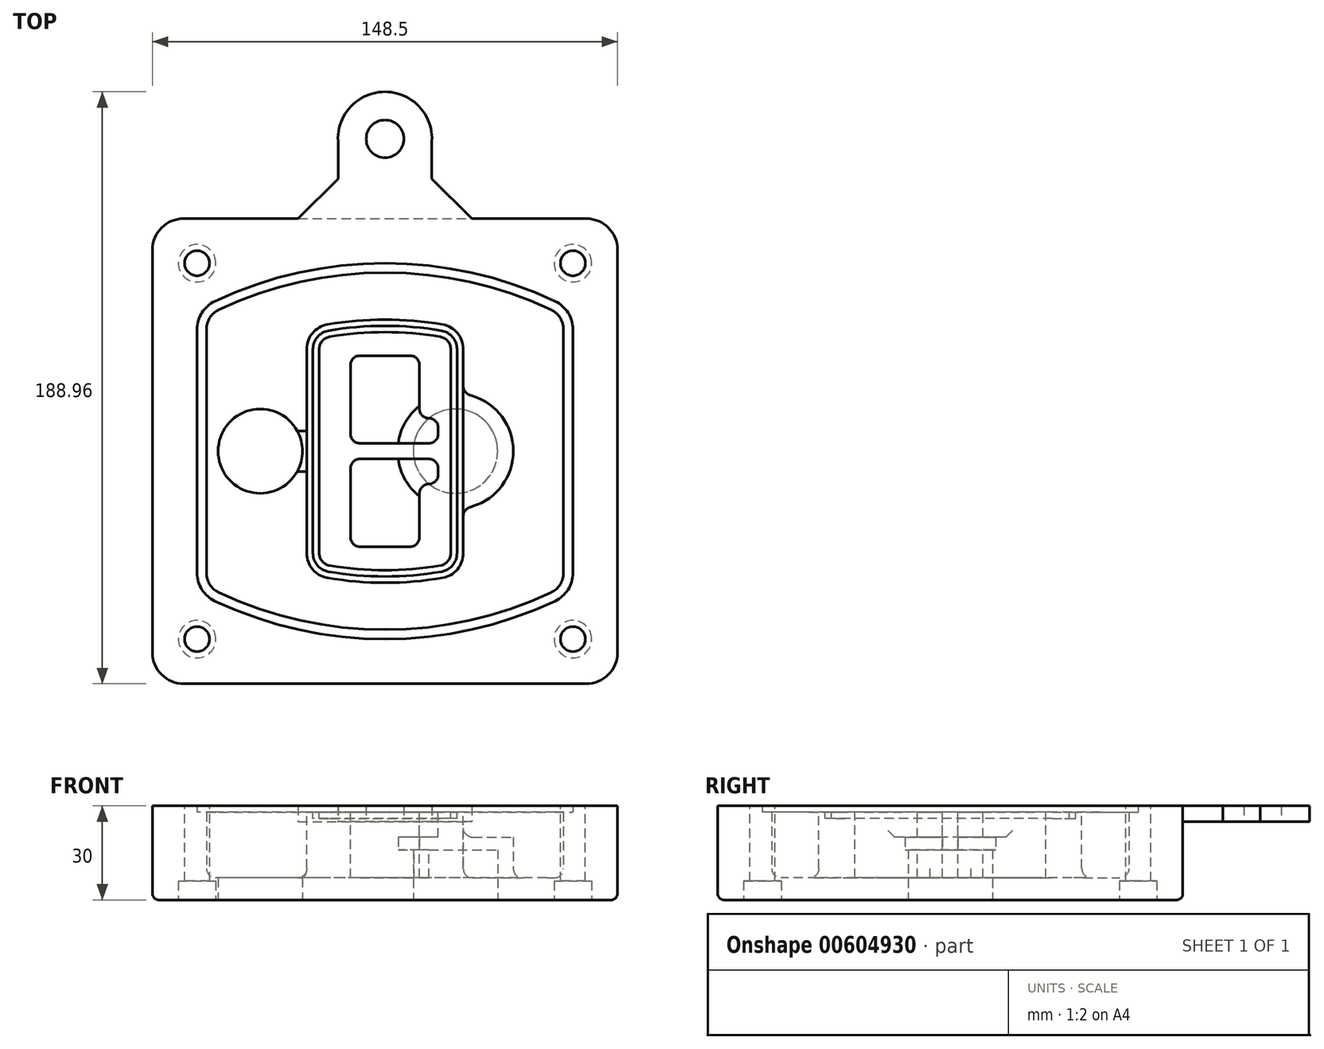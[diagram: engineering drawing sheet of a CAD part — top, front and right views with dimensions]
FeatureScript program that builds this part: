
annotation { "Feature Type Name" : "Feature", "Feature Type Description" : "" }
export const myFeature = defineFeature(function(context is Context, id is Id, definition is map)
    precondition{}
    {
        {
            var Q0;
            Q0=qCreatedBy(makeId("Top.planeOp"),FACE);
            var sketch = newSketch(context, id + "F0", { "sketchPlane" : qUnion([Q0])});
            skPoint(sketch, "E0.rect.middle", {"position": v(0, 0) * mm});
            skLineSegment(sketch, "E1.bottom", {"start": v(-64.25, -74.25) * mm, "end": v(64.25, -74.25) * mm});
            skLineSegment(sketch, "E1.top", {"start": v(-64.25, 74.25) * mm, "end": v(64.25, 74.25) * mm});
            skLineSegment(sketch, "E1.left", {"start": v(-74.25, -64.25) * mm, "end": v(-74.25, 64.25) * mm});
            skLineSegment(sketch, "E1.right", {"start": v(74.25, -64.25) * mm, "end": v(74.25, 64.25) * mm});
            skLineSegment(sketch, "E2", {"start": v(-74.25, 74.25) * mm, "end": v(74.25, -74.25) * mm, "construction": true});
            skLineSegment(sketch, "E3", {"start": v(74.25, 74.25) * mm, "end": v(-74.25, -74.25) * mm, "construction": true});
            skCircle(sketch, "E4", {"center": v(-60, 60) * mm, "radius": 4 * mm});
            skCircle(sketch, "E5", {"center": v(60, 60) * mm, "radius": 4 * mm});
            skCircle(sketch, "E6", {"center": v(60, -60) * mm, "radius": 4 * mm});
            skCircle(sketch, "E7", {"center": v(-60, -60) * mm, "radius": 4 * mm});
            skLineSegment(sketch, "E8", {"start": v(-60, 60) * mm, "end": v(60, 60) * mm, "construction": true});
            skLineSegment(sketch, "E9", {"start": v(60, 60) * mm, "end": v(60, -60) * mm, "construction": true});
            skLineSegment(sketch, "E10", {"start": v(60, -60) * mm, "end": v(-60, -60) * mm, "construction": true});
            skLineSegment(sketch, "E11", {"start": v(-60, -60) * mm, "end": v(-60, 60) * mm, "construction": true});
            skLineSegment(sketch, "E12", {"start": v(-60, 38.83) * mm, "end": v(-60, -38.83) * mm});
            skLineSegment(sketch, "E13", {"start": v(60, 38.83) * mm, "end": v(60, -38.83) * mm});
            skArc(sketch, "E14", {"start": v(54.26, 47.88) * mm, "mid": v(0, 60) * mm, "end": v(-54.26, 47.88) * mm});
            skArc(sketch, "E15", {"start": v(-54.26, -47.88) * mm, "mid": v(0, -60) * mm, "end": v(54.26, -47.88) * mm});
            skLineSegment(sketch, "E16", {"start": v(-60, 0) * mm, "end": v(60, 0) * mm, "construction": true});
            skPoint(sketch, "E17.visualSharp", {"position": v(-60, -45) * mm});
            skArc(sketch, "E17.filletArc", {"start": v(-60, -38.83) * mm, "mid": v(-58.44, -44.2) * mm, "end": v(-54.26, -47.88) * mm});
            skPoint(sketch, "E18.visualSharp", {"position": v(-60, 45) * mm});
            skArc(sketch, "E18.filletArc", {"start": v(-54.26, 47.88) * mm, "mid": v(-58.44, 44.2) * mm, "end": v(-60, 38.83) * mm});
            skPoint(sketch, "E19.visualSharp", {"position": v(60, 45) * mm});
            skArc(sketch, "E19.filletArc", {"start": v(60, 38.83) * mm, "mid": v(58.44, 44.2) * mm, "end": v(54.26, 47.88) * mm});
            skPoint(sketch, "E20.visualSharp", {"position": v(60, -45) * mm});
            skArc(sketch, "E20.filletArc", {"start": v(54.26, -47.88) * mm, "mid": v(58.44, -44.2) * mm, "end": v(60, -38.83) * mm});
            skPoint(sketch, "E21.visualSharp", {"position": v(-74.25, 74.25) * mm});
            skArc(sketch, "E21.filletArc", {"start": v(-64.25, 74.25) * mm, "mid": v(-71.32, 71.32) * mm, "end": v(-74.25, 64.25) * mm});
            skPoint(sketch, "E22.visualSharp", {"position": v(74.25, 74.25) * mm});
            skArc(sketch, "E22.filletArc", {"start": v(74.25, 64.25) * mm, "mid": v(71.32, 71.32) * mm, "end": v(64.25, 74.25) * mm});
            skPoint(sketch, "E23.visualSharp", {"position": v(74.25, -74.25) * mm});
            skArc(sketch, "E23.filletArc", {"start": v(64.25, -74.25) * mm, "mid": v(71.32, -71.32) * mm, "end": v(74.25, -64.25) * mm});
            skPoint(sketch, "E24.visualSharp", {"position": v(-74.25, -74.25) * mm});
            skArc(sketch, "E24.filletArc", {"start": v(-74.25, -64.25) * mm, "mid": v(-71.32, -71.32) * mm, "end": v(-64.25, -74.25) * mm});
            skArc(sketch, "E25.0", {"start": v(57, 38.83) * mm, "mid": v(55.9, 42.58) * mm, "end": v(52.98, 45.17) * mm});
            skLineSegment(sketch, "E25.1", {"start": v(57, 38.83) * mm, "end": v(57, -38.83) * mm});
            skArc(sketch, "E25.2", {"start": v(52.98, -45.17) * mm, "mid": v(55.9, -42.58) * mm, "end": v(57, -38.83) * mm});
            skArc(sketch, "E25.3", {"start": v(-52.98, -45.17) * mm, "mid": v(0, -57) * mm, "end": v(52.98, -45.17) * mm});
            skArc(sketch, "E25.4", {"start": v(-57, -38.83) * mm, "mid": v(-55.9, -42.58) * mm, "end": v(-52.98, -45.17) * mm});
            skArc(sketch, "E25.5", {"start": v(52.98, 45.17) * mm, "mid": v(0, 57) * mm, "end": v(-52.98, 45.17) * mm});
            skLineSegment(sketch, "E25.6", {"start": v(-57, 38.83) * mm, "end": v(-57, -38.83) * mm});
            skArc(sketch, "E25.7", {"start": v(-52.98, 45.17) * mm, "mid": v(-55.9, 42.58) * mm, "end": v(-57, 38.83) * mm});
            skArc(sketch, "E26.0", {"start": v(-55.96, 51.5) * mm, "mid": v(-61.82, 46.33) * mm, "end": v(-64, 38.83) * mm});
            skArc(sketch, "E26.1", {"start": v(55.96, 51.5) * mm, "mid": v(0, 64) * mm, "end": v(-55.96, 51.5) * mm});
            skArc(sketch, "E26.2", {"start": v(64, 38.83) * mm, "mid": v(61.82, 46.33) * mm, "end": v(55.96, 51.5) * mm});
            skLineSegment(sketch, "E26.3", {"start": v(64, 38.83) * mm, "end": v(64, -38.83) * mm});
            skArc(sketch, "E26.4", {"start": v(55.96, -51.5) * mm, "mid": v(61.82, -46.33) * mm, "end": v(64, -38.83) * mm});
            skLineSegment(sketch, "E26.5", {"start": v(-64, 38.83) * mm, "end": v(-64, -38.83) * mm});
            skArc(sketch, "E26.6", {"start": v(-55.96, -51.5) * mm, "mid": v(0, -64) * mm, "end": v(55.96, -51.5) * mm});
            skArc(sketch, "E26.7", {"start": v(-64, -38.83) * mm, "mid": v(-61.82, -46.33) * mm, "end": v(-55.96, -51.5) * mm});
            skSolve(sketch);
        }
        {
            var Q0;
            Q0=makeQuery(id+"F0.imprint","IMPRINT",FACE,{"disambiguationData":[TD([[makeQuery(id+"F0.imprint","IMPRINT",EDGE,{"derivedFrom":sQuery(id+"F0.wireOp",EDGE,"E1.bottom")}),1.0]])]});
            var Q1;
            Q1=makeQuery(id+"F0.imprint","IMPRINT",FACE,{"disambiguationData":[TD([[makeQuery(id+"F0.imprint","IMPRINT",EDGE,{"derivedFrom":sQuery(id+"F0.wireOp",EDGE,"E12")}),1.0]])]});
            var Q2;
            Q2=makeQuery(id+"F0.imprint","IMPRINT",FACE,{"disambiguationData":[TD([[makeQuery(id+"F0.imprint","IMPRINT",EDGE,{"derivedFrom":sQuery(id+"F0.wireOp",EDGE,"E25.0")}),1.0]])]});
            var Q3;
            Q3=makeQuery(id+"F0.imprint","IMPRINT",FACE,{"disambiguationData":[TD([[makeQuery(id+"F0.imprint","IMPRINT",EDGE,{"derivedFrom":sQuery(id+"F0.wireOp",EDGE,"E12")}),-1.0]])]});
            extrude(context, id + "F1", {"entities" : qUnion([Q0, Q1, Q2, Q3]), "oppositeDirection" : true, "depth" : 25 * mm});
        }
        {
            var Q0;
            Q0=makeQuery(id+"F0.imprint","IMPRINT",FACE,{"disambiguationData":[TD([[makeQuery(id+"F0.imprint","IMPRINT",EDGE,{"derivedFrom":sQuery(id+"F0.wireOp",EDGE,"E12")}),1.0]])]});
            extrude(context, id + "F2", {"entities" : qUnion([Q0]), "operationType" : NewBodyOperationType.ADD, "depth" : 3 * mm});
        }
        {
            var Q0;
            Q0=makeQuery(id+"F0.imprint","IMPRINT",FACE,{"disambiguationData":[TD([[makeQuery(id+"F0.imprint","IMPRINT",EDGE,{"derivedFrom":sQuery(id+"F0.wireOp",EDGE,"E25.0")}),1.0]])]});
            extrude(context, id + "F3", {"entities" : qUnion([Q0]), "operationType" : NewBodyOperationType.REMOVE, "oppositeDirection" : true, "depth" : 18 * mm});
        }
        {
            var Q0;
            Q0=makeQuery(id+"F2.opExtrude","CAP_FACE",FACE,{"disambiguationData":[OSD([sQuery(id+"F0.wireOp",EDGE,"E12"),sQuery(id+"F0.wireOp",EDGE,"E13"),sQuery(id+"F0.wireOp",EDGE,"E14"),sQuery(id+"F0.wireOp",EDGE,"E15"),sQuery(id+"F0.wireOp",EDGE,"E17.filletArc"),sQuery(id+"F0.wireOp",EDGE,"E18.filletArc"),sQuery(id+"F0.wireOp",EDGE,"E19.filletArc"),sQuery(id+"F0.wireOp",EDGE,"E20.filletArc"),sQuery(id+"F0.wireOp",EDGE,"E25.0"),sQuery(id+"F0.wireOp",EDGE,"E25.1"),sQuery(id+"F0.wireOp",EDGE,"E25.2"),sQuery(id+"F0.wireOp",EDGE,"E25.3"),sQuery(id+"F0.wireOp",EDGE,"E25.4"),sQuery(id+"F0.wireOp",EDGE,"E25.5"),sQuery(id+"F0.wireOp",EDGE,"E25.6"),sQuery(id+"F0.wireOp",EDGE,"E25.7")])],"isStart":false});
            var sketch = newSketch(context, id + "F4", { "sketchPlane" : qUnion([Q0])});
            skArc(sketch, "E27.0", {"start": v(-18.34, -40.45) * mm, "mid": v(0, -42) * mm, "end": v(18.34, -40.45) * mm});
            skArc(sketch, "E28.0", {"start": v(18.34, 40.45) * mm, "mid": v(0, 42) * mm, "end": v(-18.34, 40.45) * mm});
            skLineSegment(sketch, "E29", {"start": v(-25, 32.57) * mm, "end": v(-25, -32.57) * mm});
            skLineSegment(sketch, "E30", {"start": v(25, 32.57) * mm, "end": v(25, -32.57) * mm});
            skLineSegment(sketch, "E31", {"start": v(-25, 39.1) * mm, "end": v(25, 39.1) * mm, "construction": true});
            skLineSegment(sketch, "E32", {"start": v(-25, -39.1) * mm, "end": v(25, -39.1) * mm, "construction": true});
            skPoint(sketch, "E33.visualSharp", {"position": v(-25, 39.1) * mm});
            skArc(sketch, "E33.filletArc", {"start": v(-18.34, 40.45) * mm, "mid": v(-23.11, 37.73) * mm, "end": v(-25, 32.57) * mm});
            skPoint(sketch, "E34.visualSharp", {"position": v(25, 39.1) * mm});
            skArc(sketch, "E34.filletArc", {"start": v(25, 32.57) * mm, "mid": v(23.11, 37.73) * mm, "end": v(18.34, 40.45) * mm});
            skPoint(sketch, "E35.visualSharp", {"position": v(25, -39.1) * mm});
            skArc(sketch, "E35.filletArc", {"start": v(18.34, -40.45) * mm, "mid": v(23.11, -37.73) * mm, "end": v(25, -32.57) * mm});
            skPoint(sketch, "E36.visualSharp", {"position": v(-25, -39.1) * mm});
            skArc(sketch, "E36.filletArc", {"start": v(-25, -32.57) * mm, "mid": v(-23.11, -37.73) * mm, "end": v(-18.34, -40.45) * mm});
            skArc(sketch, "E37.0", {"start": v(52.98, 45.17) * mm, "mid": v(0, 57) * mm, "end": v(-52.98, 45.17) * mm});
            skArc(sketch, "E37.1", {"start": v(-52.98, 45.17) * mm, "mid": v(-55.9, 42.58) * mm, "end": v(-57, 38.83) * mm});
            skLineSegment(sketch, "E37.2", {"start": v(-57, 38.83) * mm, "end": v(-57, -38.83) * mm});
            skArc(sketch, "E37.3", {"start": v(-57, -38.83) * mm, "mid": v(-55.9, -42.58) * mm, "end": v(-52.98, -45.17) * mm});
            skArc(sketch, "E37.4", {"start": v(-52.98, -45.17) * mm, "mid": v(0, -57) * mm, "end": v(52.98, -45.17) * mm});
            skArc(sketch, "E37.5", {"start": v(52.98, -45.17) * mm, "mid": v(55.9, -42.58) * mm, "end": v(57, -38.83) * mm});
            skLineSegment(sketch, "E37.6", {"start": v(57, 38.83) * mm, "end": v(57, -38.83) * mm});
            skArc(sketch, "E37.7", {"start": v(57, 38.83) * mm, "mid": v(55.9, 42.58) * mm, "end": v(52.98, 45.17) * mm});
            skLineSegment(sketch, "E38.0", {"start": v(23, 32.57) * mm, "end": v(23, -32.57) * mm});
            skArc(sketch, "E38.1", {"start": v(18, -38.48) * mm, "mid": v(21.58, -36.44) * mm, "end": v(23, -32.57) * mm});
            skArc(sketch, "E38.2", {"start": v(-18, -38.48) * mm, "mid": v(0, -40) * mm, "end": v(18, -38.48) * mm});
            skArc(sketch, "E38.3", {"start": v(-23, -32.57) * mm, "mid": v(-21.58, -36.44) * mm, "end": v(-18, -38.48) * mm});
            skLineSegment(sketch, "E38.4", {"start": v(-23, 32.57) * mm, "end": v(-23, -32.57) * mm});
            skArc(sketch, "E38.5", {"start": v(23, 32.57) * mm, "mid": v(21.58, 36.44) * mm, "end": v(18, 38.48) * mm});
            skArc(sketch, "E38.6", {"start": v(-18, 38.48) * mm, "mid": v(-21.58, 36.44) * mm, "end": v(-23, 32.57) * mm});
            skArc(sketch, "E38.7", {"start": v(18, 38.48) * mm, "mid": v(0, 40) * mm, "end": v(-18, 38.48) * mm});
            skArc(sketch, "E39.0", {"start": v(21, 32.57) * mm, "mid": v(20.06, 35.15) * mm, "end": v(17.67, 36.5) * mm});
            skLineSegment(sketch, "E39.1", {"start": v(21, 32.57) * mm, "end": v(21, -32.57) * mm});
            skArc(sketch, "E39.2", {"start": v(17.67, -36.5) * mm, "mid": v(20.06, -35.15) * mm, "end": v(21, -32.57) * mm});
            skArc(sketch, "E39.3", {"start": v(-17.67, -36.5) * mm, "mid": v(0, -38) * mm, "end": v(17.67, -36.5) * mm});
            skArc(sketch, "E39.4", {"start": v(-21, -32.57) * mm, "mid": v(-20.06, -35.15) * mm, "end": v(-17.67, -36.5) * mm});
            skArc(sketch, "E39.5", {"start": v(17.67, 36.5) * mm, "mid": v(0, 38) * mm, "end": v(-17.67, 36.5) * mm});
            skLineSegment(sketch, "E39.6", {"start": v(-21, 32.57) * mm, "end": v(-21, -32.57) * mm});
            skArc(sketch, "E39.7", {"start": v(-17.67, 36.5) * mm, "mid": v(-20.06, 35.15) * mm, "end": v(-21, 32.57) * mm});
            skLineSegment(sketch, "E40", {"start": v(-25, 0) * mm, "end": v(25, 0) * mm, "construction": true});
            skLineSegment(sketch, "E41", {"start": v(-11, 5.5) * mm, "end": v(-11, 27.5) * mm});
            skLineSegment(sketch, "E42", {"start": v(-8, 30.5) * mm, "end": v(8, 30.5) * mm});
            skLineSegment(sketch, "E43", {"start": v(11, 27.5) * mm, "end": v(11, 13.5) * mm});
            skLineSegment(sketch, "E44", {"start": v(14, 10.5) * mm, "end": v(14, 10.5) * mm});
            skLineSegment(sketch, "E45", {"start": v(17, 7.5) * mm, "end": v(17, 5.5) * mm});
            skLineSegment(sketch, "E46", {"start": v(14, 2.5) * mm, "end": v(-8, 2.5) * mm});
            skPoint(sketch, "E47.visualSharp", {"position": v(-11, 30.5) * mm});
            skArc(sketch, "E47.filletArc", {"start": v(-8, 30.5) * mm, "mid": v(-10.12, 29.62) * mm, "end": v(-11, 27.5) * mm});
            skPoint(sketch, "E48.visualSharp", {"position": v(11, 30.5) * mm});
            skArc(sketch, "E48.filletArc", {"start": v(11, 27.5) * mm, "mid": v(10.12, 29.62) * mm, "end": v(8, 30.5) * mm});
            skPoint(sketch, "E49.visualSharp", {"position": v(11, 10.5) * mm});
            skArc(sketch, "E49.filletArc", {"start": v(11, 13.5) * mm, "mid": v(11.88, 11.38) * mm, "end": v(14, 10.5) * mm});
            skPoint(sketch, "E50.visualSharp", {"position": v(17, 10.5) * mm});
            skArc(sketch, "E50.filletArc", {"start": v(17, 7.5) * mm, "mid": v(16.12, 9.62) * mm, "end": v(14, 10.5) * mm});
            skPoint(sketch, "E51.visualSharp", {"position": v(17, 2.5) * mm});
            skArc(sketch, "E51.filletArc", {"start": v(14, 2.5) * mm, "mid": v(16.12, 3.38) * mm, "end": v(17, 5.5) * mm});
            skPoint(sketch, "E52.visualSharp", {"position": v(-11, 2.5) * mm});
            skArc(sketch, "E52.filletArc", {"start": v(-11, 5.5) * mm, "mid": v(-10.12, 3.38) * mm, "end": v(-8, 2.5) * mm});
            skLineSegment(sketch, "E53.0.MirrorCS", {"start": v(14, -2.5) * mm, "end": v(-8, -2.5) * mm});
            skArc(sketch, "E54.0.MirrorCS", {"start": v(-11, -5.5) * mm, "mid": v(-10.12, -3.38) * mm, "end": v(-8, -2.5) * mm});
            skLineSegment(sketch, "E55.0.MirrorCS", {"start": v(-11, -5.5) * mm, "end": v(-11, -27.5) * mm});
            skArc(sketch, "E56.0.MirrorCS", {"start": v(-8, -30.5) * mm, "mid": v(-10.12, -29.62) * mm, "end": v(-11, -27.5) * mm});
            skLineSegment(sketch, "E57.0.MirrorCS", {"start": v(-8, -30.5) * mm, "end": v(8, -30.5) * mm});
            skArc(sketch, "E58.0.MirrorCS", {"start": v(11, -27.5) * mm, "mid": v(10.12, -29.62) * mm, "end": v(8, -30.5) * mm});
            skLineSegment(sketch, "E59.0.MirrorCS", {"start": v(11, -27.5) * mm, "end": v(11, -13.5) * mm});
            skArc(sketch, "E60.0.MirrorCS", {"start": v(11, -13.5) * mm, "mid": v(11.88, -11.38) * mm, "end": v(14, -10.5) * mm});
            skArc(sketch, "E61.0.MirrorCS", {"start": v(17, -7.5) * mm, "mid": v(16.12, -9.62) * mm, "end": v(14, -10.5) * mm});
            skLineSegment(sketch, "E62.0.MirrorCS", {"start": v(17, -7.5) * mm, "end": v(17, -5.5) * mm});
            skArc(sketch, "E63.0.MirrorCS", {"start": v(14, -2.5) * mm, "mid": v(16.12, -3.38) * mm, "end": v(17, -5.5) * mm});
            skSolve(sketch);
        }
        {
            var Q0;
            Q0=makeQuery(id+"F4.imprint","IMPRINT",FACE,{"disambiguationData":[TD([[makeQuery(id+"F4.imprint","IMPRINT",EDGE,{"derivedFrom":sQuery(id+"F4.wireOp",EDGE,"E27.0")}),1.0]])]});
            var Q1;
            Q1=makeQuery(id+"F4.imprint","IMPRINT",FACE,{"disambiguationData":[TD([[makeQuery(id+"F4.imprint","IMPRINT",EDGE,{"derivedFrom":sQuery(id+"F4.wireOp",EDGE,"E38.0")}),-1.0]])]});
            var Q2;
            Q2=makeQuery(id+"F4.imprint","IMPRINT",FACE,{"disambiguationData":[TD([[makeQuery(id+"F4.imprint","IMPRINT",EDGE,{"derivedFrom":sQuery(id+"F4.wireOp",EDGE,"E39.0")}),1.0]])]});
            extrude(context, id + "F5", {"entities" : qUnion([Q0, Q1, Q2]), "operationType" : NewBodyOperationType.ADD, "endBound" : BoundingType.UP_TO_NEXT, "oppositeDirection" : true, "depth" : 25 * mm});
        }
        {
            var Q0;
            Q0=makeQuery(id+"F4.imprint","IMPRINT",FACE,{"disambiguationData":[TD([[makeQuery(id+"F4.imprint","IMPRINT",EDGE,{"derivedFrom":sQuery(id+"F4.wireOp",EDGE,"E38.0")}),-1.0]])]});
            extrude(context, id + "F6", {"entities" : qUnion([Q0]), "operationType" : NewBodyOperationType.REMOVE, "oppositeDirection" : true, "depth" : 2 * mm});
        }
        {
            var Q0;
            Q0=makeQuery(id+"F1.opExtrude","CAP_FACE",FACE,{"disambiguationData":[OSD([sQuery(id+"F0.wireOp",EDGE,"E1.bottom"),sQuery(id+"F0.wireOp",EDGE,"E1.top"),sQuery(id+"F0.wireOp",EDGE,"E1.left"),sQuery(id+"F0.wireOp",EDGE,"E1.right"),sQuery(id+"F0.wireOp",EDGE,"E4"),sQuery(id+"F0.wireOp",EDGE,"E5"),sQuery(id+"F0.wireOp",EDGE,"E6"),sQuery(id+"F0.wireOp",EDGE,"E7"),sQuery(id+"F0.wireOp",EDGE,"E21.filletArc"),sQuery(id+"F0.wireOp",EDGE,"E22.filletArc"),sQuery(id+"F0.wireOp",EDGE,"E23.filletArc"),sQuery(id+"F0.wireOp",EDGE,"E24.filletArc")])],"isStart":false});
            var sketch = newSketch(context, id + "F7", { "sketchPlane" : qUnion([Q0])});
            skCircle(sketch, "E64", {"center": v(22.5, 0) * mm, "radius": 13.47 * mm});
            skCircle(sketch, "E65", {"center": v(-39.81, 0) * mm, "radius": 13.47 * mm});
            skLineSegment(sketch, "E66", {"start": v(74.25, 0) * mm, "end": v(-74.25, 0) * mm});
            skCircle(sketch, "E67", {"center": v(22.5, 0) * mm, "radius": 18.47 * mm});
            skCircle(sketch, "E68", {"center": v(60, -60) * mm, "radius": 6 * mm});
            skCircle(sketch, "E69", {"center": v(-60, -60) * mm, "radius": 6 * mm});
            skCircle(sketch, "E70", {"center": v(-60, 60) * mm, "radius": 6 * mm});
            skCircle(sketch, "E71", {"center": v(60, 60) * mm, "radius": 6 * mm});
            skSolve(sketch);
        }
        {
            var Q0;
            {var subQ1=sQuery(id+"F7.wireOp",EDGE,"E66");var subQ4=sQuery(id+"F7.wireOp",EDGE,"E64");var subQ6=makeQuery(id+"F7.imprint","INTERSECT",VERTEX,{"disambiguationData":[OD(0.0)],"derivedFrom":[subQ4,subQ1]});Q0=makeQuery(id+"F7.imprint","IMPRINT",FACE,{"disambiguationData":[TD([[makeQuery(id+"F7.imprint","IMPRINT",EDGE,{"disambiguationData":[TD([[subQ6,-1.0]])],"derivedFrom":subQ4}),-1.0]])]});}
            var Q1;
            {var subQ0=sQuery(id+"F7.wireOp",EDGE,"E66");var subQ1=sQuery(id+"F7.wireOp",EDGE,"E64");var subQ3=makeQuery(id+"F7.imprint","INTERSECT",VERTEX,{"disambiguationData":[OD(0.0)],"derivedFrom":[subQ1,subQ0]});Q1=makeQuery(id+"F7.imprint","IMPRINT",FACE,{"disambiguationData":[TD([[makeQuery(id+"F7.imprint","IMPRINT",EDGE,{"disambiguationData":[TD([[subQ3,-1.0]])],"derivedFrom":subQ1}),1.0]])]});}
            var Q2;
            {var subQ0=sQuery(id+"F7.wireOp",EDGE,"E66");var subQ1=sQuery(id+"F7.wireOp",EDGE,"E64");var subQ3=makeQuery(id+"F7.imprint","INTERSECT",VERTEX,{"disambiguationData":[OD(0.0)],"derivedFrom":[subQ1,subQ0]});Q2=makeQuery(id+"F7.imprint","IMPRINT",FACE,{"disambiguationData":[TD([[makeQuery(id+"F7.imprint","IMPRINT",EDGE,{"disambiguationData":[TD([[subQ3,1.0]])],"derivedFrom":subQ1}),1.0]])]});}
            var Q3;
            {var subQ1=sQuery(id+"F7.wireOp",EDGE,"E66");var subQ4=sQuery(id+"F7.wireOp",EDGE,"E64");var subQ6=makeQuery(id+"F7.imprint","INTERSECT",VERTEX,{"disambiguationData":[OD(0.0)],"derivedFrom":[subQ4,subQ1]});Q3=makeQuery(id+"F7.imprint","IMPRINT",FACE,{"disambiguationData":[TD([[makeQuery(id+"F7.imprint","IMPRINT",EDGE,{"disambiguationData":[TD([[subQ6,1.0]])],"derivedFrom":subQ4}),-1.0]])]});}
            extrude(context, id + "F8", {"entities" : qUnion([Q0, Q1, Q2, Q3]), "operationType" : NewBodyOperationType.ADD, "oppositeDirection" : true, "depth" : 20 * mm});
        }
        {
            var Q0;
            {var subQ0=sQuery(id+"F7.wireOp",EDGE,"E66");var subQ1=sQuery(id+"F7.wireOp",EDGE,"E64");var subQ3=makeQuery(id+"F7.imprint","INTERSECT",VERTEX,{"disambiguationData":[OD(0.0)],"derivedFrom":[subQ1,subQ0]});Q0=makeQuery(id+"F7.imprint","IMPRINT",FACE,{"disambiguationData":[TD([[makeQuery(id+"F7.imprint","IMPRINT",EDGE,{"disambiguationData":[TD([[subQ3,-1.0]])],"derivedFrom":subQ1}),1.0]])]});}
            var Q1;
            {var subQ0=sQuery(id+"F7.wireOp",EDGE,"E66");var subQ1=sQuery(id+"F7.wireOp",EDGE,"E64");var subQ3=makeQuery(id+"F7.imprint","INTERSECT",VERTEX,{"disambiguationData":[OD(0.0)],"derivedFrom":[subQ1,subQ0]});Q1=makeQuery(id+"F7.imprint","IMPRINT",FACE,{"disambiguationData":[TD([[makeQuery(id+"F7.imprint","IMPRINT",EDGE,{"disambiguationData":[TD([[subQ3,1.0]])],"derivedFrom":subQ1}),1.0]])]});}
            extrude(context, id + "F9", {"entities" : qUnion([Q0, Q1]), "operationType" : NewBodyOperationType.REMOVE, "oppositeDirection" : true, "depth" : 16 * mm});
        }
        {
            var Q0;
            {var subQ0=sQuery(id+"F7.wireOp",EDGE,"E66");var subQ1=sQuery(id+"F7.wireOp",EDGE,"E65");var subQ3=makeQuery(id+"F7.imprint","INTERSECT",VERTEX,{"disambiguationData":[OD(0.0)],"derivedFrom":[subQ1,subQ0]});Q0=makeQuery(id+"F7.imprint","IMPRINT",FACE,{"disambiguationData":[TD([[makeQuery(id+"F7.imprint","IMPRINT",EDGE,{"disambiguationData":[TD([[subQ3,-1.0]])],"derivedFrom":subQ1}),1.0]])]});}
            var Q1;
            {var subQ0=sQuery(id+"F7.wireOp",EDGE,"E66");var subQ1=sQuery(id+"F7.wireOp",EDGE,"E65");var subQ3=makeQuery(id+"F7.imprint","INTERSECT",VERTEX,{"disambiguationData":[OD(0.0)],"derivedFrom":[subQ1,subQ0]});Q1=makeQuery(id+"F7.imprint","IMPRINT",FACE,{"disambiguationData":[TD([[makeQuery(id+"F7.imprint","IMPRINT",EDGE,{"disambiguationData":[TD([[subQ3,1.0]])],"derivedFrom":subQ1}),1.0]])]});}
            extrude(context, id + "F10", {"entities" : qUnion([Q0, Q1]), "operationType" : NewBodyOperationType.REMOVE, "oppositeDirection" : true, "depth" : 25 * mm});
        }
        {
            var Q0;
            Q0=makeQuery(id+"F7.imprint","IMPRINT",FACE,{"disambiguationData":[TD([[makeQuery(id+"F7.imprint","IMPRINT",EDGE,{"derivedFrom":sQuery(id+"F7.wireOp",EDGE,"E68")}),1.0]])]});
            var Q1;
            Q1=makeQuery(id+"F7.imprint","IMPRINT",FACE,{"disambiguationData":[TD([[makeQuery(id+"F7.imprint","IMPRINT",EDGE,{"derivedFrom":makeQuery(id+"F1.opExtrude","CAP_EDGE",EDGE,{"disambiguationData":[OSD([sQuery(id+"F0.wireOp",EDGE,"E5")])],"isStart":false})}),-1.0]])]});
            var Q2;
            Q2=makeQuery(id+"F7.imprint","IMPRINT",FACE,{"disambiguationData":[TD([[makeQuery(id+"F7.imprint","IMPRINT",EDGE,{"derivedFrom":sQuery(id+"F7.wireOp",EDGE,"E69")}),1.0]])]});
            var Q3;
            Q3=makeQuery(id+"F7.imprint","IMPRINT",FACE,{"disambiguationData":[TD([[makeQuery(id+"F7.imprint","IMPRINT",EDGE,{"derivedFrom":makeQuery(id+"F1.opExtrude","CAP_EDGE",EDGE,{"disambiguationData":[OSD([sQuery(id+"F0.wireOp",EDGE,"E4")])],"isStart":false})}),-1.0]])]});
            var Q4;
            Q4=makeQuery(id+"F7.imprint","IMPRINT",FACE,{"disambiguationData":[TD([[makeQuery(id+"F7.imprint","IMPRINT",EDGE,{"derivedFrom":sQuery(id+"F7.wireOp",EDGE,"E70")}),1.0]])]});
            var Q5;
            Q5=makeQuery(id+"F7.imprint","IMPRINT",FACE,{"disambiguationData":[TD([[makeQuery(id+"F7.imprint","IMPRINT",EDGE,{"derivedFrom":makeQuery(id+"F1.opExtrude","CAP_EDGE",EDGE,{"disambiguationData":[OSD([sQuery(id+"F0.wireOp",EDGE,"E7")])],"isStart":false})}),-1.0]])]});
            var Q6;
            Q6=makeQuery(id+"F7.imprint","IMPRINT",FACE,{"disambiguationData":[TD([[makeQuery(id+"F7.imprint","IMPRINT",EDGE,{"derivedFrom":sQuery(id+"F7.wireOp",EDGE,"E71")}),1.0]])]});
            var Q7;
            Q7=makeQuery(id+"F7.imprint","IMPRINT",FACE,{"disambiguationData":[TD([[makeQuery(id+"F7.imprint","IMPRINT",EDGE,{"derivedFrom":makeQuery(id+"F1.opExtrude","CAP_EDGE",EDGE,{"disambiguationData":[OSD([sQuery(id+"F0.wireOp",EDGE,"E6")])],"isStart":false})}),-1.0]])]});
            extrude(context, id + "F11", {"entities" : qUnion([Q0, Q1, Q2, Q3, Q4, Q5, Q6, Q7]), "operationType" : NewBodyOperationType.REMOVE, "oppositeDirection" : true, "depth" : 6 * mm});
        }
        {
            var Q0;
            Q0=makeQuery(id+"F9.boolean.opBoolean","COPY",FACE,{"derivedFrom":makeQuery(id+"F9.opExtrude","CAP_FACE",FACE,{"disambiguationData":[OSD([sQuery(id+"F7.wireOp",EDGE,"E64")])],"isStart":false})});
            var sketch = newSketch(context, id + "F12", { "sketchPlane" : qUnion([Q0])});
            skArc(sketch, "E72.0", {"start": v(11, 14.45) * mm, "mid": v(6.45, 9.13) * mm, "end": v(4.2, 2.5) * mm});
            skArc(sketch, "E72.1", {"start": v(4.2, -2.5) * mm, "mid": v(6.45, -9.13) * mm, "end": v(11, -14.45) * mm});
            skLineSegment(sketch, "E73", {"start": v(4.2, -2.5) * mm, "end": v(14, -2.5) * mm});
            skLineSegment(sketch, "E74.0", {"start": v(14, 2.5) * mm, "end": v(4.2, 2.5) * mm});
            skArc(sketch, "E74.1", {"start": v(14, 2.5) * mm, "mid": v(16.12, 3.38) * mm, "end": v(17, 5.5) * mm});
            skLineSegment(sketch, "E74.2", {"start": v(17, 7.5) * mm, "end": v(17, 5.5) * mm});
            skArc(sketch, "E74.3", {"start": v(17, 7.5) * mm, "mid": v(16.12, 9.62) * mm, "end": v(14, 10.5) * mm});
            skArc(sketch, "E74.4", {"start": v(11, 13.5) * mm, "mid": v(11.88, 11.38) * mm, "end": v(14, 10.5) * mm});
            skLineSegment(sketch, "E74.5", {"start": v(11, 14.45) * mm, "end": v(11, 13.5) * mm});
            skLineSegment(sketch, "E74.7", {"start": v(14, -2.5) * mm, "end": v(4.2, -2.5) * mm});
            skArc(sketch, "E74.8", {"start": v(14, -2.5) * mm, "mid": v(16.12, -3.38) * mm, "end": v(17, -5.5) * mm});
            skLineSegment(sketch, "E74.9", {"start": v(17, -7.5) * mm, "end": v(17, -5.5) * mm});
            skArc(sketch, "E74.10", {"start": v(17, -7.5) * mm, "mid": v(16.12, -9.62) * mm, "end": v(14, -10.5) * mm});
            skArc(sketch, "E74.11", {"start": v(11, -13.5) * mm, "mid": v(11.88, -11.38) * mm, "end": v(14, -10.5) * mm});
            skLineSegment(sketch, "E74.12", {"start": v(11, -14.45) * mm, "end": v(11, -13.5) * mm});
            skPoint(sketch, "E75.orphan", {"position": v(11, -27.5) * mm});
            skPoint(sketch, "E76.orphan", {"position": v(-8, -2.5) * mm});
            skPoint(sketch, "E77.orphan", {"position": v(-8, 2.5) * mm});
            skPoint(sketch, "E78.orphan", {"position": v(11, 27.5) * mm});
            skSolve(sketch);
        }
        {
            var Q0;
            {var subQ7=sQuery(id+"F12.wireOp",EDGE,"E72.0");var subQ14=sQuery(id+"F12.wireOp",EDGE,"E72.1");var subQ16=sQuery(id+"F12.wireOp",EDGE,"E74.1");var subQ18=sQuery(id+"F12.wireOp",EDGE,"E74.8");Q0=qUnion([makeQuery(id+"F12.imprint","IMPRINT",FACE,{"disambiguationData":[TD([[makeQuery(id+"F12.imprint","IMPRINT",EDGE,{"derivedFrom":subQ7}),1.0]])]}),makeQuery(id+"F12.imprint","IMPRINT",FACE,{"disambiguationData":[TD([[makeQuery(id+"F12.imprint","IMPRINT",EDGE,{"derivedFrom":subQ14}),1.0]])]}),makeQuery(id+"F12.imprint","IMPRINT",FACE,{"disambiguationData":[TD([[makeQuery(id+"F12.imprint","IMPRINT",EDGE,{"derivedFrom":subQ16}),1.0]])]}),makeQuery(id+"F12.imprint","IMPRINT",FACE,{"disambiguationData":[TD([[makeQuery(id+"F12.imprint","IMPRINT",EDGE,{"derivedFrom":subQ18}),-1.0]])]})]);}
            var Q1;
            Q1=makeQuery(id+"F5.boolean.opBoolean","SPLIT",FACE,{"disambiguationData":[TD([makeQuery(id+"F5.opExtrude","SWEPT_FACE",FACE,{"disambiguationData":[OSD([sQuery(id+"F4.wireOp",EDGE,"E41")])]})])],"derivedFrom":makeQuery(id+"F3.boolean.opBoolean","COPY",FACE,{"derivedFrom":makeQuery(id+"F3.opExtrude","CAP_FACE",FACE,{"disambiguationData":[OSD([sQuery(id+"F0.wireOp",EDGE,"E25.0"),sQuery(id+"F0.wireOp",EDGE,"E25.1"),sQuery(id+"F0.wireOp",EDGE,"E25.2"),sQuery(id+"F0.wireOp",EDGE,"E25.3"),sQuery(id+"F0.wireOp",EDGE,"E25.4"),sQuery(id+"F0.wireOp",EDGE,"E25.5"),sQuery(id+"F0.wireOp",EDGE,"E25.6"),sQuery(id+"F0.wireOp",EDGE,"E25.7")])],"isStart":false})})});
            extrude(context, id + "F13", {"entities" : qUnion([Q0]), "operationType" : NewBodyOperationType.REMOVE, "endBound" : BoundingType.UP_TO_SURFACE, "endBoundEntityFace" : qUnion([Q1]), "depth" : 25 * mm});
        }
        {
            var Q0;
            Q0=makeQuery(id+"F3.boolean.opBoolean","COPY",EDGE,{"derivedFrom":makeQuery(id+"F3.opExtrude","CAP_EDGE",EDGE,{"disambiguationData":[OSD([sQuery(id+"F0.wireOp",EDGE,"E25.6")])],"isStart":false})});
            var Q1;
            Q1=makeQuery(id+"F8.boolean.opBoolean","INTERSECT",EDGE,{"derivedFrom":[makeQuery(id+"F5.opExtrude","SWEPT_FACE",FACE,{"disambiguationData":[OSD([sQuery(id+"F4.wireOp",EDGE,"E30")])]}),makeQuery(id+"F8.opExtrude","CAP_FACE",FACE,{"disambiguationData":[OSD([sQuery(id+"F7.wireOp",EDGE,"E67")])],"isStart":false})]});
            var Q2;
            Q2=makeQuery(id+"F8.boolean.opBoolean","INTERSECT",EDGE,{"disambiguationData":[OD(1.0)],"derivedFrom":[makeQuery(id+"F5.opExtrude","SWEPT_FACE",FACE,{"disambiguationData":[OSD([sQuery(id+"F4.wireOp",EDGE,"E30")])]}),makeQuery(id+"F8.opExtrude","SWEPT_FACE",FACE,{"disambiguationData":[OSD([sQuery(id+"F7.wireOp",EDGE,"E67")])]})]});
            var Q3;
            {var subQ0=sQuery(id+"F4.wireOp",EDGE,"E30");Q3=makeQuery(id+"F8.boolean.opBoolean","SPLIT",EDGE,{"disambiguationData":[TD([makeQuery(id+"F5.opExtrude","SWEPT_FACE",FACE,{"disambiguationData":[OSD([sQuery(id+"F4.wireOp",EDGE,"E35.filletArc")])]})])],"derivedFrom":makeQuery(id+"F5.opExtrude","CAP_EDGE",EDGE,{"disambiguationData":[OSD([subQ0])],"isStart":false})});}
            var Q4;
            {var subQ0=sQuery(id+"F0.wireOp",EDGE,"E25.7");var subQ1=sQuery(id+"F0.wireOp",EDGE,"E25.1");var subQ2=sQuery(id+"F0.wireOp",EDGE,"E25.6");var subQ3=sQuery(id+"F0.wireOp",EDGE,"E25.5");var subQ4=sQuery(id+"F0.wireOp",EDGE,"E25.4");var subQ5=sQuery(id+"F0.wireOp",EDGE,"E25.0");var subQ6=sQuery(id+"F0.wireOp",EDGE,"E25.2");var subQ7=sQuery(id+"F0.wireOp",EDGE,"E25.3");Q4=makeQuery(id+"F8.boolean.opBoolean","INTERSECT",EDGE,{"derivedFrom":[makeQuery(id+"F5.boolean.opBoolean","SPLIT",FACE,{"disambiguationData":[TD([makeQuery(id+"F2.opExtrude","SWEPT_FACE",FACE,{"disambiguationData":[OSD([subQ5])]})])],"derivedFrom":makeQuery(id+"F3.boolean.opBoolean","COPY",FACE,{"derivedFrom":makeQuery(id+"F3.opExtrude","CAP_FACE",FACE,{"disambiguationData":[OSD([subQ5,subQ1,subQ6,subQ7,subQ4,subQ3,subQ2,subQ0])],"isStart":false})})}),makeQuery(id+"F8.opExtrude","SWEPT_FACE",FACE,{"disambiguationData":[OSD([sQuery(id+"F7.wireOp",EDGE,"E67")])]})]});}
            var Q5;
            Q5=makeQuery(id+"F8.boolean.opBoolean","INTERSECT",EDGE,{"disambiguationData":[OD(0.0)],"derivedFrom":[makeQuery(id+"F5.opExtrude","SWEPT_FACE",FACE,{"disambiguationData":[OSD([sQuery(id+"F4.wireOp",EDGE,"E30")])]}),makeQuery(id+"F8.opExtrude","SWEPT_FACE",FACE,{"disambiguationData":[OSD([sQuery(id+"F7.wireOp",EDGE,"E67")])]})]});
            fillet(context, id + "F14", {"entities" : qUnion([Q0, Q1, Q2, Q3, Q4, Q5]), "radius" : 3 * mm, "tangentPropagation" : true, "allowEdgeOverflow" : false});
        }
        {
            var Q0;
            Q0=makeQuery(id+"F1.opExtrude","CAP_EDGE",EDGE,{"disambiguationData":[OSD([sQuery(id+"F0.wireOp",EDGE,"E1.bottom")])],"isStart":false});
            fillet(context, id + "F15", {"entities" : qUnion([Q0]), "radius" : 2 * mm, "tangentPropagation" : true, "allowEdgeOverflow" : false});
        }
        {
            var Q0;
            {var subQ0=sQuery(id+"F0.wireOp",EDGE,"E21.filletArc");var subQ1=sQuery(id+"F0.wireOp",EDGE,"E7");var subQ2=sQuery(id+"F0.wireOp",EDGE,"E6");var subQ3=sQuery(id+"F0.wireOp",EDGE,"E5");var subQ4=sQuery(id+"F0.wireOp",EDGE,"E4");var subQ5=sQuery(id+"F0.wireOp",EDGE,"E22.filletArc");var subQ6=sQuery(id+"F0.wireOp",EDGE,"E1.bottom");var subQ7=sQuery(id+"F0.wireOp",EDGE,"E1.right");var subQ8=sQuery(id+"F0.wireOp",EDGE,"E1.top");var subQ9=sQuery(id+"F0.wireOp",EDGE,"E1.left");var subQ10=sQuery(id+"F0.wireOp",EDGE,"E23.filletArc");var subQ11=sQuery(id+"F0.wireOp",EDGE,"E24.filletArc");Q0=makeQuery(id+"F2.boolean.opBoolean","SPLIT",FACE,{"disambiguationData":[TD([makeQuery(id+"F1.opExtrude","SWEPT_FACE",FACE,{"disambiguationData":[OSD([subQ6])]})])],"derivedFrom":makeQuery(id+"F1.opExtrude","CAP_FACE",FACE,{"disambiguationData":[OSD([subQ6,subQ8,subQ9,subQ7,subQ4,subQ3,subQ2,subQ1,subQ0,subQ5,subQ10,subQ11])],"isStart":true})});}
            var sketch = newSketch(context, id + "F16", { "sketchPlane" : qUnion([Q0])});
            skSolve(sketch);
        }
        {
            var Q0;
            Q0=makeQuery(id+"F16.imprint","IMPRINT",FACE,{"disambiguationData":[TD([[makeQuery(id+"F16.imprint","IMPRINT",EDGE,{"derivedFrom":makeQuery(id+"F1.opExtrude","CAP_EDGE",EDGE,{"disambiguationData":[OSD([sQuery(id+"F0.wireOp",EDGE,"E1.bottom")])],"isStart":true})}),1.0]])]});
            var sketch = newSketch(context, id + "F17", { "sketchPlane" : qUnion([Q0])});
            skLineSegment(sketch, "E79", {"start": v(-27.71, 74.25) * mm, "end": v(-14.98, 86.98) * mm});
            skLineSegment(sketch, "E80", {"start": v(27.71, 74.25) * mm, "end": v(14.98, 86.98) * mm});
            skLineSegment(sketch, "E81", {"start": v(-14.98, 86.98) * mm, "end": v(-14.98, 98.98) * mm});
            skLineSegment(sketch, "E82", {"start": v(14.98, 86.98) * mm, "end": v(14.98, 98.98) * mm});
            skArc(sketch, "E83", {"start": v(14.98, 98.98) * mm, "mid": v(0, 114.7) * mm, "end": v(-14.98, 98.98) * mm});
            skCircle(sketch, "E84", {"center": v(0, 99.7) * mm, "radius": 6 * mm});
            skLineSegment(sketch, "E85", {"start": v(-74.5, 0) * mm, "end": v(74.18, 0) * mm, "construction": true});
            skLineSegment(sketch, "E86.MirrorCS", {"start": v(-14.98, -86.98) * mm, "end": v(-14.98, -98.98) * mm});
            skLineSegment(sketch, "E87.MirrorCS", {"start": v(-27.71, -74.25) * mm, "end": v(-14.98, -86.98) * mm});
            skArc(sketch, "E88.MirrorCS", {"start": v(14.98, -98.98) * mm, "mid": v(0, -114.7) * mm, "end": v(-14.98, -98.98) * mm});
            skCircle(sketch, "E89.MirrorC", {"center": v(0, -99.7) * mm, "radius": 6 * mm});
            skLineSegment(sketch, "E90.MirrorCS", {"start": v(14.98, -86.98) * mm, "end": v(14.98, -98.98) * mm});
            skLineSegment(sketch, "E91.MirrorCS", {"start": v(27.71, -74.25) * mm, "end": v(14.98, -86.98) * mm});
            skSolve(sketch);
        }
        {
            var Q0;
            {var subQ0=sQuery(id+"F17.wireOp",EDGE,"E79");Q0=makeQuery(id+"F17.imprint","IMPRINT",FACE,{"disambiguationData":[TD([[makeQuery(id+"F17.imprint","IMPRINT",EDGE,{"derivedFrom":subQ0}),-1.0]])]});}
            var Q1;
            Q1=makeQuery(id+"F16.imprint","IMPRINT",FACE,{"disambiguationData":[TD([[makeQuery(id+"F16.imprint","IMPRINT",EDGE,{"derivedFrom":makeQuery(id+"F1.opExtrude","CAP_EDGE",EDGE,{"disambiguationData":[OSD([sQuery(id+"F0.wireOp",EDGE,"E1.bottom")])],"isStart":true})}),1.0]])]});
            extrude(context, id + "F18", {"entities" : qUnion([Q0, Q1]), "operationType" : NewBodyOperationType.ADD, "depth" : 5 * mm, "offsetDistance" : 25 * mm});
        }
    });
